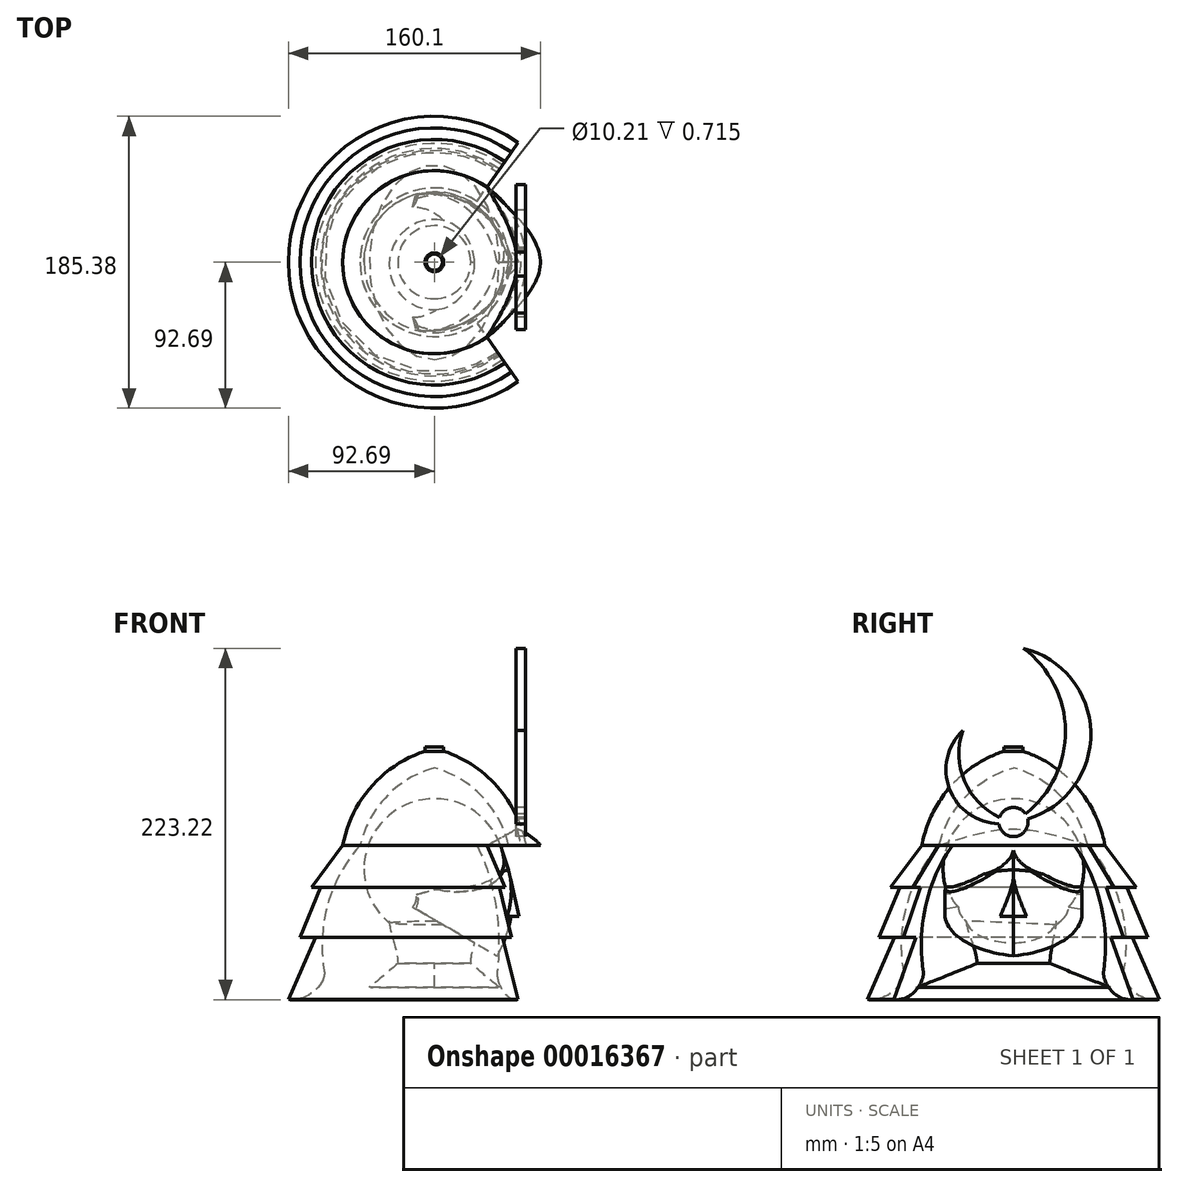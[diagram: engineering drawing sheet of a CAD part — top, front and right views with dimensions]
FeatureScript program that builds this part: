
annotation { "Feature Type Name" : "Feature", "Feature Type Description" : "" }
export const myFeature = defineFeature(function(context is Context, id is Id, definition is map)
    precondition{}
    {
        {
            var Q0;
            Q0=qCreatedBy(makeId("Top.planeOp"),FACE);
            var sketch = newSketch(context, id + "F0", { "sketchPlane" : qUnion([Q0])});
            skArc(sketch, "E0", {"start": v(-44.68, 0) * mm, "mid": v(0, -44.68) * mm, "end": v(44.68, 0) * mm});
            skLineSegment(sketch, "E1", {"start": v(44.68, 0) * mm, "end": v(-44.68, 0) * mm});
            skLineSegment(sketch, "E2", {"start": v(44.68, 0) * mm, "end": v(44.68, 36.03) * mm, "construction": true});
            skSolve(sketch);
        }
        {
            var Q0;
            Q0 = qSketchRegion(id + "F0", true);
            var Q1;
            Q1=sQuery(id+"F0.wireOp",EDGE,"E1");
            revolve(context, id + "F1", {"entities" : qUnion([Q0]), "axis" : qUnion([Q1]), "revolveType" : RevolveType.FULL});
        }
        {
            var Q0;
            Q0=makeQuery(id+"F1.opRevolve","SWEPT_BODY",BODY,{"disambiguationData":[OSD([sQuery(id+"F0.wireOp",EDGE,"E0"),sQuery(id+"F0.wireOp",EDGE,"E1")])]});
            var Q1;
            Q1=qCreatedBy(makeId("Top.planeOp"),FACE);
            transform(context, id + "F2", {"entities" : qUnion([Q0]), "transformType" : TransformType.TRANSLATION_DISTANCE, "transformDirection" : qUnion([Q1]), "distance" : 15 * mm, "oppositeDirection" : true, "makeCopy" : false});
        }
        {
            var Q0;
            Q0=qCreatedBy(makeId("Top.planeOp"),FACE);
            var sketch = newSketch(context, id + "F3", { "sketchPlane" : qUnion([Q0])});
            skLineSegment(sketch, "E3", {"start": v(0, 0) * mm, "end": v(12.34, -43.08) * mm});
            skArc(sketch, "E4", {"start": v(12.34, -43.08) * mm, "mid": v(50.67, -33.3) * mm, "end": v(72.02, 0) * mm});
            skLineSegment(sketch, "E5.MirrorCS", {"start": v(0, 0) * mm, "end": v(12.34, 43.08) * mm});
            skLineSegment(sketch, "E6.MirrorCS", {"start": v(12.34, 43.08) * mm, "end": v(12.34, 43.08) * mm});
            skArc(sketch, "E7.MirrorCS", {"start": v(12.34, 43.08) * mm, "mid": v(50.67, 33.3) * mm, "end": v(72.02, 0) * mm});
            skLineSegment(sketch, "E8", {"start": v(0, -61.4) * mm, "end": v(0, 61.38) * mm, "construction": true});
            skPoint(sketch, "E9", {"position": v(42.07, 0) * mm});
            skSolve(sketch);
        }
        {
            var Q0;
            Q0 = qSketchRegion(id + "F3", true);
            var Q1;
            Q1=sQuery(id+"F3.wireOp",EDGE,"E8");
            revolve(context, id + "F4", {"entities" : qUnion([Q0]), "axis" : qUnion([Q1]), "revolveType" : RevolveType.ONE_DIRECTION, "angle" : 45 * degree});
        }
        {
            var Q0;
            Q0=makeQuery(id+"F4.opRevolve","SWEPT_BODY",BODY,{"disambiguationData":[OSD([sQuery(id+"F3.wireOp",EDGE,"E3"),sQuery(id+"F3.wireOp",EDGE,"17598f5f-404b-4f8c-ac35-278ca7a2c35a"),sQuery(id+"F3.wireOp",EDGE,"E4"),sQuery(id+"F3.wireOp",EDGE,"5336d24a-33b8-4873-b715-2a8792ee797a"),sQuery(id+"F3.wireOp",EDGE,"E5.MirrorCS"),sQuery(id+"F3.wireOp",EDGE,"E6.MirrorCS"),sQuery(id+"F3.wireOp",EDGE,"E7.MirrorCS"),sQuery(id+"F3.wireOp",EDGE,"d338a3b0-5d36-45a3-872c-7f8dcec3f61b0.MirrorCS")])]});
            var Q1;
            Q1=sQuery(id+"F3.wireOp",EDGE,"E8");
            var Q2;
            Q2=qCreatedBy(makeId("Top.planeOp"),FACE);
            transform(context, id + "F5", {"entities" : qUnion([Q0]), "transformType" : TransformType.TRANSLATION_DISTANCE, "transformDirection" : qUnion([Q2]), "distance" : 15.56 * mm, "oppositeDirection" : true, "makeCopy" : false});
        }
        {
            var Q0;
            Q0=makeQuery(id+"F4.opRevolve","SWEPT_BODY",BODY,{"disambiguationData":[OSD([sQuery(id+"F3.wireOp",EDGE,"E3"),sQuery(id+"F3.wireOp",EDGE,"17598f5f-404b-4f8c-ac35-278ca7a2c35a"),sQuery(id+"F3.wireOp",EDGE,"E4"),sQuery(id+"F3.wireOp",EDGE,"5336d24a-33b8-4873-b715-2a8792ee797a"),sQuery(id+"F3.wireOp",EDGE,"E5.MirrorCS"),sQuery(id+"F3.wireOp",EDGE,"E6.MirrorCS"),sQuery(id+"F3.wireOp",EDGE,"E7.MirrorCS"),sQuery(id+"F3.wireOp",EDGE,"d338a3b0-5d36-45a3-872c-7f8dcec3f61b0.MirrorCS")])]});
            var Q1;
            Q1=qCreatedBy(makeId("Right.planeOp"),FACE);
            transform(context, id + "F6", {"entities" : qUnion([Q0]), "transformType" : TransformType.TRANSLATION_DISTANCE, "transformDirection" : qUnion([Q1]), "distance" : 29.06 * mm, "oppositeDirection" : true, "makeCopy" : false});
        }
        {
            var Q0;
            Q0=makeQuery(id+"F4.opRevolve","SWEPT_BODY",BODY,{"disambiguationData":[OSD([sQuery(id+"F3.wireOp",EDGE,"E3"),sQuery(id+"F3.wireOp",EDGE,"E4"),sQuery(id+"F3.wireOp",EDGE,"E5.MirrorCS"),sQuery(id+"F3.wireOp",EDGE,"E7.MirrorCS")])]});
            var Q1;
            Q1=sQuery(id+"F0.wireOp",EDGE,"E2");
            transform(context, id + "F7", {"entities" : qUnion([Q0]), "transformType" : TransformType.ROTATION, "transformAxis" : qUnion([Q1]), "angle" : 15 * degree, "oppositeDirection" : true, "makeCopy" : false});
        }
        {
            var Q0;
            Q0=makeQuery(id+"F1.opRevolve","SWEPT_BODY",BODY,{"disambiguationData":[OSD([sQuery(id+"F0.wireOp",EDGE,"E0"),sQuery(id+"F0.wireOp",EDGE,"E1")])]});
            var Q1;
            Q1=makeQuery(id+"F4.opRevolve","SWEPT_BODY",BODY,{"disambiguationData":[OSD([sQuery(id+"F3.wireOp",EDGE,"E3"),sQuery(id+"F3.wireOp",EDGE,"17598f5f-404b-4f8c-ac35-278ca7a2c35a"),sQuery(id+"F3.wireOp",EDGE,"E4"),sQuery(id+"F3.wireOp",EDGE,"5336d24a-33b8-4873-b715-2a8792ee797a"),sQuery(id+"F3.wireOp",EDGE,"E5.MirrorCS"),sQuery(id+"F3.wireOp",EDGE,"E6.MirrorCS"),sQuery(id+"F3.wireOp",EDGE,"E7.MirrorCS"),sQuery(id+"F3.wireOp",EDGE,"d338a3b0-5d36-45a3-872c-7f8dcec3f61b0.MirrorCS")])]});
            booleanBodies(context, id + "F8", {"operationType" : BooleanOperationType.UNION, "tools" : qUnion([Q0, Q1])});
        }
        {
            var Q0;
            Q0=qCreatedBy(makeId("Front.planeOp"),FACE);
            var sketch = newSketch(context, id + "F9", { "sketchPlane" : qUnion([Q0])});
            skLineSegment(sketch, "E10", {"start": v(-75.5, -58.39) * mm, "end": v(-92.69, -97.86) * mm});
            skLineSegment(sketch, "E11", {"start": v(0, 63.89) * mm, "end": v(0, -69.8) * mm, "construction": true});
            skLineSegment(sketch, "E12", {"start": v(-72.2, -26.73) * mm, "end": v(-85.33, -58.39) * mm});
            skLineSegment(sketch, "E13", {"start": v(-85.33, -58.39) * mm, "end": v(-75.5, -58.39) * mm});
            skLineSegment(sketch, "E14", {"start": v(-58.16, 0) * mm, "end": v(-78.04, -26.73) * mm});
            skLineSegment(sketch, "E15", {"start": v(-78.04, -26.73) * mm, "end": v(-72.2, -26.73) * mm});
            skLineSegment(sketch, "E16", {"start": v(-47.17, 0) * mm, "end": v(-58.16, 0) * mm});
            skArc(sketch, "E17", {"start": v(-47.17, 0) * mm, "mid": v(-67.66, -37.09) * mm, "end": v(-69.99, -79.4) * mm});
            skArc(sketch, "E18", {"start": v(-92.69, -97.86) * mm, "mid": v(-79.74, -95.06) * mm, "end": v(-70.78, -85.3) * mm});
            skPoint(sketch, "E19.visualSharp", {"position": v(-69.53, -81.9) * mm});
            skArc(sketch, "E19.filletArc", {"start": v(-70.78, -85.3) * mm, "mid": v(-69.93, -82.4) * mm, "end": v(-69.99, -79.4) * mm});
            skSolve(sketch);
        }
        {
            var Q0;
            {var subQ6=sQuery(id+"F9.wireOp",EDGE,"bed17606-2d73-4af0-a236-4f785531fa8f");Q0=makeQuery(id+"F9.imprint","IMPRINT",FACE,{"disambiguationData":[TD([[makeQuery(id+"F9.imprint","IMPRINT",EDGE,{"derivedFrom":subQ6}),1.0]])]});}
            var Q1;
            {var subQ3=sQuery(id+"F9.wireOp",EDGE,"3992ad86-beb6-407e-abb3-2c1991481c55");Q1=makeQuery(id+"F9.imprint","IMPRINT",FACE,{"disambiguationData":[TD([[makeQuery(id+"F9.imprint","IMPRINT",EDGE,{"derivedFrom":subQ3}),1.0]])]});}
            var Q2;
            {var subQ3=sQuery(id+"F9.wireOp",EDGE,"4294b020-6c44-4885-9173-856c7b450247");Q2=makeQuery(id+"F9.imprint","IMPRINT",FACE,{"disambiguationData":[TD([[makeQuery(id+"F9.imprint","IMPRINT",EDGE,{"derivedFrom":subQ3}),1.0]])]});}
            var Q3;
            {var subQ7=sQuery(id+"F9.wireOp",EDGE,"4294b020-6c44-4885-9173-856c7b450247");Q3=makeQuery(id+"F9.imprint","IMPRINT",FACE,{"disambiguationData":[TD([[makeQuery(id+"F9.imprint","IMPRINT",EDGE,{"derivedFrom":subQ7}),-1.0]])]});}
            var Q4;
            {var subQ2=sQuery(id+"F9.wireOp",EDGE,"3992ad86-beb6-407e-abb3-2c1991481c55");Q4=makeQuery(id+"F9.imprint","IMPRINT",FACE,{"disambiguationData":[TD([[makeQuery(id+"F9.imprint","IMPRINT",EDGE,{"derivedFrom":subQ2}),-1.0]])]});}
            var Q5;
            {var subQ0=sQuery(id+"F9.wireOp",EDGE,"E13");var subQ3=sQuery(id+"F9.wireOp",EDGE,"E12");var subQ4=makeQuery(id+"F9.imprint","INTERSECT",VERTEX,{"derivedFrom":[subQ3,subQ0]});Q5=makeQuery(id+"F9.imprint","IMPRINT",FACE,{"disambiguationData":[TD([[makeQuery(id+"F9.imprint","IMPRINT",EDGE,{"disambiguationData":[TD([[subQ4,-1.0]])],"derivedFrom":subQ0}),1.0]])]});}
            var Q6;
            {var subQ0=sQuery(id+"F9.wireOp",EDGE,"E15");var subQ3=sQuery(id+"F9.wireOp",EDGE,"E14");var subQ4=makeQuery(id+"F9.imprint","INTERSECT",VERTEX,{"derivedFrom":[subQ3,subQ0]});Q6=makeQuery(id+"F9.imprint","IMPRINT",FACE,{"disambiguationData":[TD([[makeQuery(id+"F9.imprint","IMPRINT",EDGE,{"disambiguationData":[TD([[subQ4,-1.0]])],"derivedFrom":subQ0}),1.0]])]});}
            var Q7;
            Q7=sQuery(id+"F9.wireOp",EDGE,"E11");
            revolve(context, id + "F10", {"entities" : qUnion([Q0, Q1, Q2, Q3, Q4, Q5, Q6]), "axis" : qUnion([Q7]), "revolveType" : RevolveType.SYMMETRIC, "angle" : 250 * degree});
        }
        {
            var Q0;
            Q0=qCreatedBy(makeId("Right.planeOp"),FACE);
            var sketch = newSketch(context, id + "F11", { "sketchPlane" : qUnion([Q0])});
            skArc(sketch, "E20", {"start": v(0, 61.56) * mm, "mid": v(-38.19, 39.4) * mm, "end": v(-58.14, 0) * mm});
            skArc(sketch, "E21", {"start": v(0, 49.28) * mm, "mid": v(-30.36, 31.11) * mm, "end": v(-47.2, 0) * mm});
            skLineSegment(sketch, "E22", {"start": v(0, 61.56) * mm, "end": v(0, 49.28) * mm});
            skLineSegment(sketch, "E23", {"start": v(-58.14, 0) * mm, "end": v(-47.2, 0) * mm});
            skSolve(sketch);
        }
        {
            var Q0;
            Q0=makeQuery(id+"F11.imprint","IMPRINT",FACE,{"disambiguationData":[TD([[makeQuery(id+"F11.imprint","IMPRINT",EDGE,{"derivedFrom":sQuery(id+"F11.wireOp",EDGE,"E20")}),1.0]])]});
            var Q1;
            Q1=sQuery(id+"F11.wireOp",EDGE,"E22");
            revolve(context, id + "F12", {"entities" : qUnion([Q0]), "axis" : qUnion([Q1]), "revolveType" : RevolveType.FULL});
        }
        {
            var Q0;
            Q0=qCreatedBy(makeId("Right.planeOp"),FACE);
            var sketch = newSketch(context, id + "F13", { "sketchPlane" : qUnion([Q0])});
            skArc(sketch, "E24", {"start": v(-32.22, 58.1) * mm, "mid": v(-38.56, 16.6) * mm, "end": v(0, 0) * mm});
            skArc(sketch, "E25", {"start": v(-32.22, 58.1) * mm, "mid": v(-29.07, 21.86) * mm, "end": v(0, 0) * mm});
            skCircle(sketch, "E26", {"center": v(0, 0) * mm, "radius": 9.26 * mm});
            skArc(sketch, "E27", {"start": v(0, 0) * mm, "mid": v(49.07, 52.54) * mm, "end": v(6.38, 110.39) * mm});
            skArc(sketch, "E28", {"start": v(0, 0) * mm, "mid": v(32.95, 53.47) * mm, "end": v(6.38, 110.39) * mm});
            skSolve(sketch);
        }
        {
            var Q0;
            Q0 = qSketchRegion(id + "F13", true);
            extrude(context, id + "F14", {"entities" : qUnion([Q0]), "depth" : 6 * mm});
        }
        {
            var Q0;
            Q0=makeQuery(id+"F14.opExtrude","SWEPT_BODY",BODY,{"disambiguationData":[OSD([sQuery(id+"F13.wireOp",EDGE,"63a4e0e8-54da-4c7c-8e49-798323a95d9c0.MirrorCS"),sQuery(id+"F13.wireOp",EDGE,"63a4e0e8-54da-4c7c-8e49-798323a95d9c1.MirrorCS"),sQuery(id+"F13.wireOp",EDGE,"63a4e0e8-54da-4c7c-8e49-798323a95d9c2.MirrorCS"),sQuery(id+"F13.wireOp",EDGE,"63a4e0e8-54da-4c7c-8e49-798323a95d9c3.MirrorCS"),sQuery(id+"F13.wireOp",EDGE,"63a4e0e8-54da-4c7c-8e49-798323a95d9c4.MirrorCS"),sQuery(id+"F13.wireOp",EDGE,"63a4e0e8-54da-4c7c-8e49-798323a95d9c5.MirrorCS")])]});
            var Q1;
            Q1=makeQuery(id+"F14.opExtrude","SWEPT_BODY",BODY,{"disambiguationData":[OSD([sQuery(id+"F13.wireOp",EDGE,"E24"),sQuery(id+"F13.wireOp",EDGE,"b7e1e591-e3d9-4fc4-9fd9-ac906eb5375b"),sQuery(id+"F13.wireOp",EDGE,"b3045065-7fd3-4527-97a0-abc5098df0ba"),sQuery(id+"F13.wireOp",EDGE,"015c9c46-c47a-4591-99de-78b190910ab0"),sQuery(id+"F13.wireOp",EDGE,"8cbf14fa-2419-4e41-a801-432650f1cecd"),sQuery(id+"F13.wireOp",EDGE,"E25")])]});
            var Q2;
            Q2=qCreatedBy(makeId("Right.planeOp"),FACE);
            transform(context, id + "F15", {"entities" : qUnion([Q0, Q1]), "transformType" : TransformType.TRANSLATION_DISTANCE, "transformDirection" : qUnion([Q2]), "distance" : 51.95 * mm, "makeCopy" : false});
        }
        {
            var Q0;
            Q0=qCreatedBy(makeId("Front.planeOp"),FACE);
            var sketch = newSketch(context, id + "F16", { "sketchPlane" : qUnion([Q0])});
            skLineSegment(sketch, "E29.bottom", {"start": v(0, 62.6) * mm, "end": v(-5.96, 62.6) * mm});
            skLineSegment(sketch, "E29.top", {"start": v(0, 58.52) * mm, "end": v(-5.96, 58.52) * mm});
            skLineSegment(sketch, "E29.left", {"start": v(0, 62.6) * mm, "end": v(0, 58.52) * mm});
            skLineSegment(sketch, "E29.right", {"start": v(-5.96, 62.6) * mm, "end": v(-5.96, 58.52) * mm});
            skLineSegment(sketch, "E30.bottom", {"start": v(-5.1, 62.9) * mm, "end": v(1.24, 62.9) * mm});
            skLineSegment(sketch, "E30.top", {"start": v(-5.1, 61.9) * mm, "end": v(1.24, 61.9) * mm});
            skLineSegment(sketch, "E30.left", {"start": v(-5.1, 62.9) * mm, "end": v(-5.1, 61.9) * mm});
            skLineSegment(sketch, "E30.right", {"start": v(1.24, 62.9) * mm, "end": v(1.24, 61.9) * mm});
            skSolve(sketch);
        }
        {
            var Q0;
            {var subQ8=sQuery(id+"F16.wireOp",EDGE,"E29.top");Q0=makeQuery(id+"F16.imprint","IMPRINT",FACE,{"disambiguationData":[TD([[makeQuery(id+"F16.imprint","IMPRINT",EDGE,{"derivedFrom":subQ8}),-1.0]])]});}
            var Q1;
            Q1=sQuery(id+"F11.wireOp",EDGE,"E22");
            revolve(context, id + "F17", {"operationType" : NewBodyOperationType.ADD, "entities" : qUnion([Q0]), "axis" : qUnion([Q1]), "revolveType" : RevolveType.FULL});
        }
        {
            var Q0;
            Q0=makeQuery(id+"F14.opExtrude","SWEPT_BODY",BODY,{"disambiguationData":[OSD([sQuery(id+"F13.wireOp",EDGE,"E24"),sQuery(id+"F13.wireOp",EDGE,"b7e1e591-e3d9-4fc4-9fd9-ac906eb5375b"),sQuery(id+"F13.wireOp",EDGE,"b3045065-7fd3-4527-97a0-abc5098df0ba"),sQuery(id+"F13.wireOp",EDGE,"015c9c46-c47a-4591-99de-78b190910ab0"),sQuery(id+"F13.wireOp",EDGE,"8cbf14fa-2419-4e41-a801-432650f1cecd"),sQuery(id+"F13.wireOp",EDGE,"E25"),sQuery(id+"F13.wireOp",EDGE,"63a4e0e8-54da-4c7c-8e49-798323a95d9c0.MirrorCS"),sQuery(id+"F13.wireOp",EDGE,"63a4e0e8-54da-4c7c-8e49-798323a95d9c1.MirrorCS"),sQuery(id+"F13.wireOp",EDGE,"63a4e0e8-54da-4c7c-8e49-798323a95d9c2.MirrorCS"),sQuery(id+"F13.wireOp",EDGE,"63a4e0e8-54da-4c7c-8e49-798323a95d9c3.MirrorCS"),sQuery(id+"F13.wireOp",EDGE,"63a4e0e8-54da-4c7c-8e49-798323a95d9c4.MirrorCS"),sQuery(id+"F13.wireOp",EDGE,"63a4e0e8-54da-4c7c-8e49-798323a95d9c5.MirrorCS"),sQuery(id+"F13.wireOp",EDGE,"E26")])]});
            var Q1;
            Q1=qCreatedBy(makeId("Top.planeOp"),FACE);
            transform(context, id + "F18", {"entities" : qUnion([Q0]), "transformType" : TransformType.TRANSLATION_DISTANCE, "transformDirection" : qUnion([Q1]), "distance" : 14.88 * mm, "makeCopy" : false});
        }
        {
            var Q0;
            Q0=qCreatedBy(makeId("Front.planeOp"),FACE);
            var sketch = newSketch(context, id + "F19", { "sketchPlane" : qUnion([Q0])});
            skLineSegment(sketch, "E31", {"start": v(67.4, 0.05) * mm, "end": v(55, 0.05) * mm});
            skLineSegment(sketch, "E32", {"start": v(55, 0.05) * mm, "end": v(52.48, 10.4) * mm});
            skArc(sketch, "E33", {"start": v(67.4, 0.05) * mm, "mid": v(60.62, 6.2) * mm, "end": v(52.48, 10.4) * mm});
            skSolve(sketch);
        }
        {
            var Q0;
            Q0=makeQuery(id+"F10.opRevolve","CAP_VERTEX",VERTEX,{"disambiguationData":[OSD([sQuery(id+"F9.wireOp",EDGE,"E14"),sQuery(id+"F9.wireOp",EDGE,"E16")])],"isStart":true});
            var Q1;
            Q1=makeQuery(id+"F19.imprint","IMPRINT",FACE,{"disambiguationData":[TD([[makeQuery(id+"F19.imprint","IMPRINT",EDGE,{"derivedFrom":sQuery(id+"F19.wireOp",EDGE,"E31")}),-1.0]])]});
            var Q2;
            Q2=makeQuery(id+"F10.opRevolve","CAP_VERTEX",VERTEX,{"disambiguationData":[OSD([sQuery(id+"F9.wireOp",EDGE,"E14"),sQuery(id+"F9.wireOp",EDGE,"E16")])],"isStart":false});
            loft(context, id + "F20", {"sheetProfilesArray" : [{ "sheetProfileEntities" : qUnion([Q0]) }, { "sheetProfileEntities" : qUnion([Q1]) }, { "sheetProfileEntities" : qUnion([Q2]) }]});
        }
        {
            var Q0;
            Q0=qCreatedBy(makeId("Top.planeOp"),FACE);
            cPlane(context, id + "F21", {"entities" : qUnion([Q0]), "cplaneType" : CPlaneType.OFFSET, "offset" : 90 * mm, "oppositeDirection" : true, "width" : 150 * mm, "height" : 150 * mm});
        }
        {
            var Q0;
            Q0=qCreatedBy(id+"F21.planeOp",FACE);
            var sketch = newSketch(context, id + "F22", { "sketchPlane" : qUnion([Q0])});
            skEllipse(sketch, "E34", {"center": v(0, 0) * mm, "majorRadius": 61.75 * mm, "minorRadius": 41.4 * mm, "majorAxis": v(0, -1)});
            skSolve(sketch);
        }
        {
            var Q0;
            Q0=qCreatedBy(id+"F21.planeOp",FACE);
            cPlane(context, id + "F23", {"entities" : qUnion([Q0]), "cplaneType" : CPlaneType.OFFSET, "offset" : 15 * mm, "width" : 150 * mm, "height" : 150 * mm});
        }
        {
            var Q0;
            Q0=qCreatedBy(id+"F23.planeOp",FACE);
            var sketch = newSketch(context, id + "F24", { "sketchPlane" : qUnion([Q0])});
            skCircle(sketch, "E35", {"center": v(0, 0) * mm, "radius": 23.2 * mm});
            skSolve(sketch);
        }
        {
            var Q0;
            Q0=qCreatedBy(id+"F23.planeOp",FACE);
            cPlane(context, id + "F25", {"entities" : qUnion([Q0]), "cplaneType" : CPlaneType.OFFSET, "offset" : 30 * mm, "width" : 150 * mm, "height" : 150 * mm});
        }
        {
            var Q0;
            Q0=qCreatedBy(id+"F25.planeOp",FACE);
            var sketch = newSketch(context, id + "F26", { "sketchPlane" : qUnion([Q0])});
            skCircle(sketch, "E36", {"center": v(0, -1.42) * mm, "radius": 28.98 * mm});
            skArc(sketch, "E37", {"start": v(33.36, -9.72) * mm, "mid": v(45.44, -8.86) * mm, "end": v(53.7, 0) * mm});
            skArc(sketch, "E38.MirrorCS", {"start": v(33.36, 9.72) * mm, "mid": v(45.44, 8.86) * mm, "end": v(53.7, 0) * mm});
            skLineSegment(sketch, "E39", {"start": v(33.36, -9.72) * mm, "end": v(33.36, 9.72) * mm});
            skSolve(sketch);
        }
        {
            var Q1;
            {var subQ0=sQuery(id+"F3.wireOp",EDGE,"E4");var subQ1=sQuery(id+"F3.wireOp",EDGE,"E7.MirrorCS");Q1=makeQuery(id+"F8.opBoolean","SPLIT",FACE,{"disambiguationData":[TD([makeQuery(id+"F1.opRevolve","SWEPT_FACE",FACE,{"disambiguationData":[OSD([sQuery(id+"F0.wireOp",EDGE,"E0")])]}),makeQuery(id+"F4.opRevolve","SWEPT_FACE",FACE,{"disambiguationData":[OSD([subQ0])]}),makeQuery(id+"F4.opRevolve","SWEPT_FACE",FACE,{"disambiguationData":[OSD([subQ1])]})])],"derivedFrom":makeQuery(id+"F4.opRevolve","CAP_FACE",FACE,{"disambiguationData":[OSD([sQuery(id+"F3.wireOp",EDGE,"E3"),subQ0,sQuery(id+"F3.wireOp",EDGE,"E5.MirrorCS"),subQ1])],"isStart":true})});}
            var Q2;
            Q2=sQuery(id+"F3.wireOp",VERTEX,"E9");
            loft(context, id + "F27", {"operationType" : NewBodyOperationType.ADD, "sheetProfilesArray" : [{ "sheetProfileEntities" : qUnion([Q1]) }, { "sheetProfileEntities" : qUnion([Q2]) }]});
        }
        {
            var Q0;
            Q0=makeQuery(id+"F8.opBoolean","INTERSECT",EDGE,{"derivedFrom":[makeQuery(id+"F1.opRevolve","SWEPT_FACE",FACE,{"disambiguationData":[OSD([sQuery(id+"F0.wireOp",EDGE,"E0")])]}),makeQuery(id+"F4.opRevolve","SWEPT_FACE",FACE,{"disambiguationData":[OSD([sQuery(id+"F3.wireOp",EDGE,"E7.MirrorCS")])]})]});
            var Q1;
            Q1=makeQuery(id+"F8.opBoolean","INTERSECT",EDGE,{"derivedFrom":[makeQuery(id+"F1.opRevolve","SWEPT_FACE",FACE,{"disambiguationData":[OSD([sQuery(id+"F0.wireOp",EDGE,"E0")])]}),makeQuery(id+"F4.opRevolve","SWEPT_FACE",FACE,{"disambiguationData":[OSD([sQuery(id+"F3.wireOp",EDGE,"E4")])]})]});
            fillet(context, id + "F28", {"entities" : qUnion([Q0, Q1]), "radius" : 10 * mm, "tangentPropagation" : true, "allowEdgeOverflow" : false});
        }
        {
            var Q1;
            Q1=makeQuery(id+"F26.imprint","IMPRINT",FACE,{"disambiguationData":[TD([[makeQuery(id+"F26.imprint","IMPRINT",EDGE,{"derivedFrom":sQuery(id+"F26.wireOp",EDGE,"E37")}),1.0]])]});
            var Q2;
            {var subQ0=sQuery(id+"F3.wireOp",EDGE,"E4");var subQ1=sQuery(id+"F3.wireOp",EDGE,"E7.MirrorCS");Q2=makeQuery(id+"F27.boolean.opBoolean","MERGE",VERTEX,{"derivedFrom":[makeQuery(id+"F4.opRevolve","CAP_VERTEX",VERTEX,{"disambiguationData":[OSD([subQ0,subQ1])],"isStart":true}),makeQuery(id+"F27.opLoft","MID_CAP_VERTEX",VERTEX,{"disambiguationData":[OSD([subQ0,subQ1])],"capPos":0.0})]});}
            loft(context, id + "F29", {"operationType" : NewBodyOperationType.ADD, "sheetProfilesArray" : [{ "sheetProfileEntities" : qUnion([Q1]) }, { "sheetProfileEntities" : qUnion([Q2]) }]});
        }
        {
            var Q0;
            Q0=makeQuery(id+"F22.imprint","IMPRINT",FACE,{"disambiguationData":[TD([[makeQuery(id+"F22.imprint","IMPRINT",EDGE,{"derivedFrom":sQuery(id+"F22.wireOp",EDGE,"E34")}),1.0]])]});
            var Q1;
            Q1=makeQuery(id+"F24.imprint","IMPRINT",FACE,{"disambiguationData":[TD([[makeQuery(id+"F24.imprint","IMPRINT",EDGE,{"derivedFrom":sQuery(id+"F24.wireOp",EDGE,"E35")}),1.0]])]});
            loft(context, id + "F30", {"startCondition" : LoftEndDerivativeType.TANGENT_TO_PROFILE, "startMagnitude" : 0.1, "sheetProfilesArray" : [{ "sheetProfileEntities" : qUnion([Q0]) }, { "sheetProfileEntities" : qUnion([Q1]) }]});
        }
        {
            var Q1;
            Q1=makeQuery(id+"F24.imprint","IMPRINT",FACE,{"disambiguationData":[TD([[makeQuery(id+"F24.imprint","IMPRINT",EDGE,{"derivedFrom":sQuery(id+"F24.wireOp",EDGE,"E35")}),1.0]])]});
            var Q2;
            Q2=makeQuery(id+"F26.imprint","IMPRINT",FACE,{"disambiguationData":[TD([[makeQuery(id+"F26.imprint","IMPRINT",EDGE,{"derivedFrom":sQuery(id+"F26.wireOp",EDGE,"E36")}),1.0]])]});
            loft(context, id + "F31", {"operationType" : NewBodyOperationType.ADD, "startCondition" : LoftEndDerivativeType.NORMAL_TO_PROFILE, "startMagnitude" : 1, "endCondition" : LoftEndDerivativeType.NORMAL_TO_PROFILE, "endMagnitude" : 1, "sheetProfilesArray" : [{ "sheetProfileEntities" : qUnion([Q1]) }, { "sheetProfileEntities" : qUnion([Q2]) }]});
        }
    });
